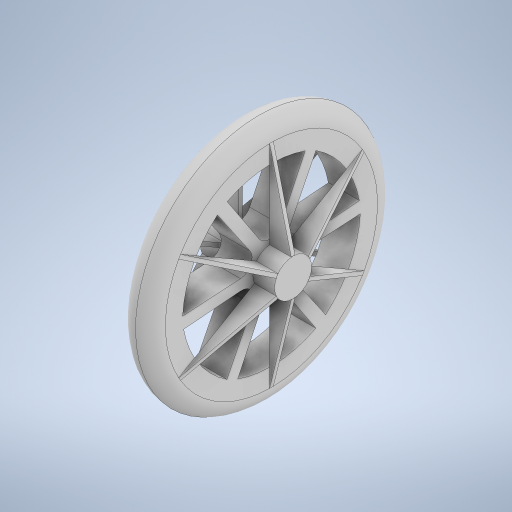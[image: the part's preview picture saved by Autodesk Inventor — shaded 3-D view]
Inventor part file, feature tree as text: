
AUTODESK INVENTOR PART (.ipt)
format: ipt  version: 2023 (Build 270158000, 158)  size: 449,024 bytes
history: native  units: in
note: dims shown in document units (in); Inventor stores cm internally (conversion verified against a paired STEP export)
features: extrude x4, sketch x4, pattern_circular x2, fillet x2, mirror x1, plane x1
ambient origin geometry x8: Origin, YZ Plane, XZ Plane, XY Plane, X Axis, Y Axis, Z Axis, Center Point
bodies: Solid1 (feature_tree)
feature tree (14):
  extrude  "Extrusion1"  Depth=0.9843in
  extrude  "Extrusion2"  Depth=0.689in TaperAngle=0.0deg
  extrude  "Extrusion3"  Depth=3.1496in
  pattern_circular  "Circular Pattern1"  [2 undecoded]
  fillet  "Fillet1"  Radius=3.1496in
  fillet  "Fillet2"  Radius=0.9843in
  extrude  "Extrusion4"  Depth=2.3622in TaperAngle=360.0deg
  pattern_circular  "Circular Pattern2"  [2 undecoded]
  mirror  "Mirror1"
  sketch  "Sketch1"  dims[d0=0.9843in d1=0.0in d2=7.874in]
  sketch  "Sketch2"  dims[d3=1.1811in d4=0.689in d5=1.6732in d6=0.0in d7=0.0in]
  sketch  "Sketch3"  dims[d8=3.1496in d10=3.1496in]
  sketch  "Sketch4"  dims[d12=60.0deg d14=0.3937in d15=3.1496in d16=0.9843in d17=0.0in d18=2.3622in d19=360.0deg d21=0.5906in d22=0.5906in d23=0.1181in d24=0.0in d25=2.3622in d26=360.0deg]
  plane  "Work Plane1"
note: 4 required parameter values undecoded (feature->parameter linkage not recoverable at this tier; creation-order binding heuristic only, values carry confidence <= 0.55)
